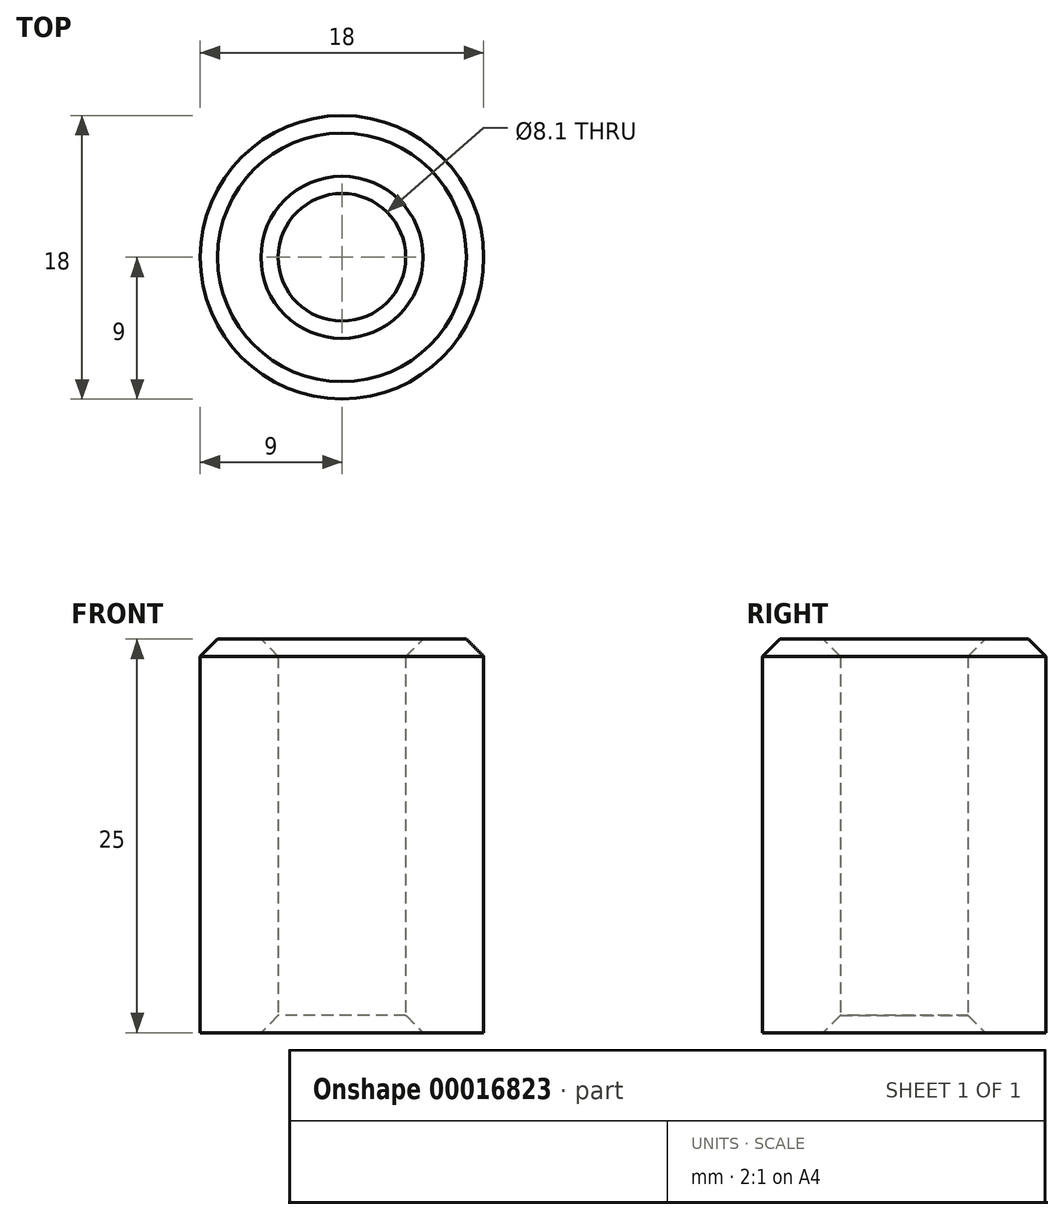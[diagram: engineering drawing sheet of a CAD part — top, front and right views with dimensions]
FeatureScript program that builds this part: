
annotation { "Feature Type Name" : "Feature", "Feature Type Description" : "" }
export const myFeature = defineFeature(function(context is Context, id is Id, definition is map)
    precondition{}
    {
        {
            var Q0;
            Q0=qCreatedBy(makeId("Top.planeOp"),FACE);
            var sketch = newSketch(context, id + "F0", { "sketchPlane" : qUnion([Q0])});
            skCircle(sketch, "E0", {"center": v(0, 0) * mm, "radius": 9 * mm});
            skCircle(sketch, "E1", {"center": v(0, 0) * mm, "radius": 4.05 * mm});
            skSolve(sketch);
        }
        {
            var Q0;
            Q0 = qSketchRegion(id + "F0", true);
            extrude(context, id + "F1", {"entities" : qUnion([Q0]), "depth" : 25 * mm});
        }
        {
            var Q0;
            Q0=makeQuery(id+"F1.opExtrude","CAP_EDGE",EDGE,{"disambiguationData":[OSD([sQuery(id+"F0.wireOp",EDGE,"E1")])],"isStart":false});
            var Q1;
            Q1=makeQuery(id+"F1.opExtrude","CAP_EDGE",EDGE,{"disambiguationData":[OSD([sQuery(id+"F0.wireOp",EDGE,"E0")])],"isStart":false});
            var Q2;
            Q2=makeQuery(id+"F1.opExtrude","CAP_EDGE",EDGE,{"disambiguationData":[OSD([sQuery(id+"F0.wireOp",EDGE,"E1")])],"isStart":true});
            chamfer(context, id + "F2", {"entities" : qUnion([Q0, Q1, Q2]), "width" : 1.1 * mm, "tangentPropagation" : true});
        }
    });
